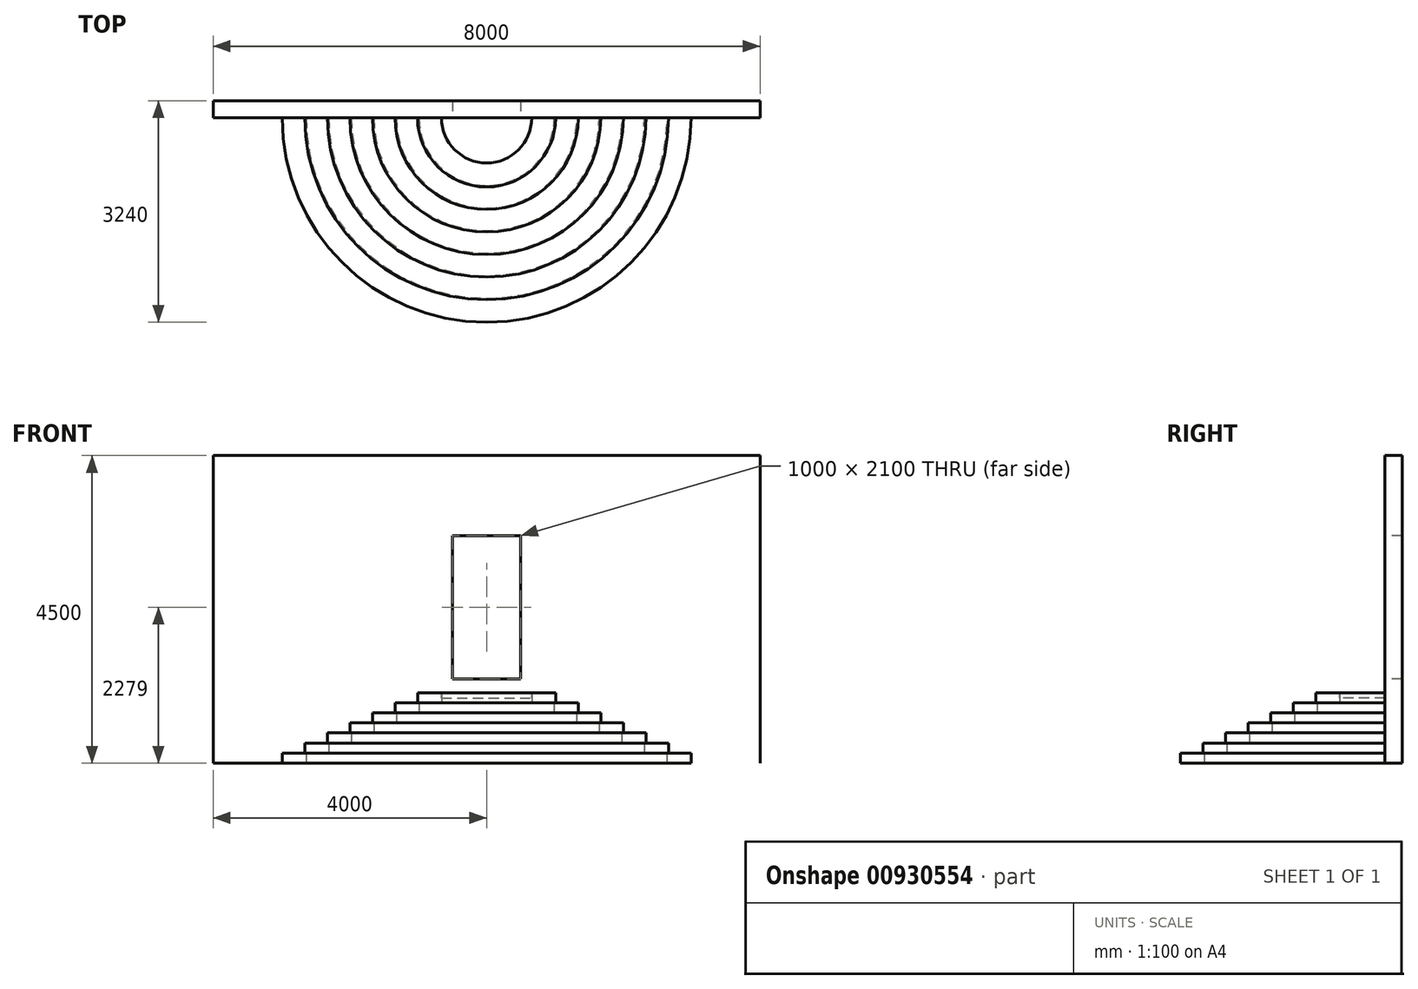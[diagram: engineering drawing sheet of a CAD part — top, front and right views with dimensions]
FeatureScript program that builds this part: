
annotation { "Feature Type Name" : "Feature", "Feature Type Description" : "" }
export const myFeature = defineFeature(function(context is Context, id is Id, definition is map)
    precondition{}
    {
        {
            var Q0;
            Q0=qCreatedBy(makeId("Top.planeOp"),FACE);
            var sketch = newSketch(context, id + "F0", { "sketchPlane" : qUnion([Q0])});
            skArc(sketch, "E0", {"start": v(-2990, 0) * mm, "mid": v(0, -2990) * mm, "end": v(2990, 0) * mm});
            skArc(sketch, "E1", {"start": v(-2640, 0) * mm, "mid": v(0, -2640) * mm, "end": v(2640, 0) * mm});
            skLineSegment(sketch, "E2", {"start": v(-2990, 0) * mm, "end": v(-2640, 0) * mm});
            skLineSegment(sketch, "E3", {"start": v(2640, 0) * mm, "end": v(2990, 0) * mm});
            skSolve(sketch);
        }
        {
            var Q0;
            Q0 = qSketchRegion(id + "F0", true);
            extrude(context, id + "F1", {"entities" : qUnion([Q0]), "depth" : 147 * mm, "offsetDistance" : 25 * mm});
        }
        {
            var Q0;
            Q0=makeQuery(id+"F1.opExtrude","CAP_FACE",FACE,{"disambiguationData":[OSD([sQuery(id+"F0.wireOp",EDGE,"E0"),sQuery(id+"F0.wireOp",EDGE,"E1"),sQuery(id+"F0.wireOp",EDGE,"E2"),sQuery(id+"F0.wireOp",EDGE,"E3")])],"isStart":false});
            var sketch = newSketch(context, id + "F2", { "sketchPlane" : qUnion([Q0])});
            skArc(sketch, "E4", {"start": v(-2660, 0) * mm, "mid": v(0, -2660) * mm, "end": v(2660, 0) * mm});
            skArc(sketch, "E5", {"start": v(-2310, 0) * mm, "mid": v(0, -2310) * mm, "end": v(2310, 0) * mm});
            skLineSegment(sketch, "E6", {"start": v(-2660, 0) * mm, "end": v(-2310, 0) * mm});
            skLineSegment(sketch, "E7", {"start": v(2310, 0) * mm, "end": v(2660, 0) * mm});
            skSolve(sketch);
        }
        {
            var Q0;
            Q0 = qSketchRegion(id + "F2", true);
            extrude(context, id + "F3", {"entities" : qUnion([Q0]), "operationType" : NewBodyOperationType.ADD, "depth" : 147 * mm, "offsetDistance" : 25 * mm});
        }
        {
            var Q0;
            Q0=makeQuery(id+"F3.opExtrude","CAP_FACE",FACE,{"disambiguationData":[OSD([sQuery(id+"F2.wireOp",EDGE,"E4"),sQuery(id+"F2.wireOp",EDGE,"E5"),sQuery(id+"F2.wireOp",EDGE,"E6"),sQuery(id+"F2.wireOp",EDGE,"E7")])],"isStart":false});
            var sketch = newSketch(context, id + "F4", { "sketchPlane" : qUnion([Q0])});
            skArc(sketch, "E8", {"start": v(-2330, 0) * mm, "mid": v(0, -2330) * mm, "end": v(2330, 0) * mm});
            skArc(sketch, "E9", {"start": v(-1980, 0) * mm, "mid": v(0, -1980) * mm, "end": v(1980, 0) * mm});
            skLineSegment(sketch, "E10", {"start": v(-2330, 0) * mm, "end": v(-1980, 0) * mm});
            skLineSegment(sketch, "E11", {"start": v(1980, 0) * mm, "end": v(2330, 0) * mm});
            skSolve(sketch);
        }
        {
            var Q0;
            Q0 = qSketchRegion(id + "F4", true);
            extrude(context, id + "F5", {"entities" : qUnion([Q0]), "operationType" : NewBodyOperationType.ADD, "depth" : 147 * mm, "offsetDistance" : 25 * mm});
        }
        {
            var Q0;
            Q0=makeQuery(id+"F5.opExtrude","CAP_FACE",FACE,{"disambiguationData":[OSD([sQuery(id+"F4.wireOp",EDGE,"E8"),sQuery(id+"F4.wireOp",EDGE,"E9"),sQuery(id+"F4.wireOp",EDGE,"E10"),sQuery(id+"F4.wireOp",EDGE,"E11")])],"isStart":false});
            var sketch = newSketch(context, id + "F6", { "sketchPlane" : qUnion([Q0])});
            skArc(sketch, "E12", {"start": v(-2000, 0) * mm, "mid": v(0, -2000) * mm, "end": v(2000, 0) * mm});
            skArc(sketch, "E13", {"start": v(-1650, 0) * mm, "mid": v(0, -1650) * mm, "end": v(1650, 0) * mm});
            skLineSegment(sketch, "E14", {"start": v(-2000, 0) * mm, "end": v(-1650, 0) * mm});
            skLineSegment(sketch, "E15", {"start": v(1650, 0) * mm, "end": v(2000, 0) * mm});
            skSolve(sketch);
        }
        {
            var Q0;
            Q0 = qSketchRegion(id + "F6", true);
            extrude(context, id + "F7", {"entities" : qUnion([Q0]), "operationType" : NewBodyOperationType.ADD, "depth" : 147 * mm, "offsetDistance" : 25 * mm});
        }
        {
            var Q0;
            Q0=makeQuery(id+"F7.opExtrude","CAP_FACE",FACE,{"disambiguationData":[OSD([sQuery(id+"F6.wireOp",EDGE,"E12"),sQuery(id+"F6.wireOp",EDGE,"E13"),sQuery(id+"F6.wireOp",EDGE,"E14"),sQuery(id+"F6.wireOp",EDGE,"E15")])],"isStart":false});
            var sketch = newSketch(context, id + "F8", { "sketchPlane" : qUnion([Q0])});
            skArc(sketch, "E16", {"start": v(-1670, 0) * mm, "mid": v(0, -1670) * mm, "end": v(1670, 0) * mm});
            skArc(sketch, "E17", {"start": v(-1320, 0) * mm, "mid": v(0, -1320) * mm, "end": v(1320, 0) * mm});
            skLineSegment(sketch, "E18", {"start": v(-1670, 0) * mm, "end": v(-1320, 0) * mm});
            skLineSegment(sketch, "E19", {"start": v(1320, 0) * mm, "end": v(1670, 0) * mm});
            skSolve(sketch);
        }
        {
            var Q0;
            Q0 = qSketchRegion(id + "F8", true);
            extrude(context, id + "F9", {"entities" : qUnion([Q0]), "operationType" : NewBodyOperationType.ADD, "depth" : 147 * mm, "offsetDistance" : 25 * mm});
        }
        {
            var Q0;
            Q0=makeQuery(id+"F9.opExtrude","CAP_FACE",FACE,{"disambiguationData":[OSD([sQuery(id+"F8.wireOp",EDGE,"E16"),sQuery(id+"F8.wireOp",EDGE,"E17"),sQuery(id+"F8.wireOp",EDGE,"E18"),sQuery(id+"F8.wireOp",EDGE,"E19")])],"isStart":false});
            var sketch = newSketch(context, id + "F10", { "sketchPlane" : qUnion([Q0])});
            skArc(sketch, "E20", {"start": v(-1340, 0) * mm, "mid": v(0, -1340) * mm, "end": v(1340, 0) * mm});
            skArc(sketch, "E21", {"start": v(-990, 0) * mm, "mid": v(0, -990) * mm, "end": v(990, 0) * mm});
            skLineSegment(sketch, "E22", {"start": v(-1340, 0) * mm, "end": v(-990, 0) * mm});
            skLineSegment(sketch, "E23", {"start": v(990, 0) * mm, "end": v(1340, 0) * mm});
            skSolve(sketch);
        }
        {
            var Q0;
            Q0 = qSketchRegion(id + "F10", true);
            extrude(context, id + "F11", {"entities" : qUnion([Q0]), "operationType" : NewBodyOperationType.ADD, "depth" : 147 * mm, "offsetDistance" : 25 * mm});
        }
        {
            var Q0;
            Q0=makeQuery(id+"F11.opExtrude","CAP_FACE",FACE,{"disambiguationData":[OSD([sQuery(id+"F10.wireOp",EDGE,"E20"),sQuery(id+"F10.wireOp",EDGE,"E21"),sQuery(id+"F10.wireOp",EDGE,"E22"),sQuery(id+"F10.wireOp",EDGE,"E23")])],"isStart":false});
            var sketch = newSketch(context, id + "F12", { "sketchPlane" : qUnion([Q0])});
            skArc(sketch, "E24", {"start": v(-1010, 0) * mm, "mid": v(0, -1010) * mm, "end": v(1010, 0) * mm});
            skArc(sketch, "E25", {"start": v(-660, 0) * mm, "mid": v(0, -660) * mm, "end": v(660, 0) * mm});
            skLineSegment(sketch, "E26", {"start": v(-1010, 0) * mm, "end": v(-660, 0) * mm});
            skLineSegment(sketch, "E27", {"start": v(660, 0) * mm, "end": v(1010, 0) * mm});
            skSolve(sketch);
        }
        {
            var Q0;
            Q0 = qSketchRegion(id + "F12", true);
            extrude(context, id + "F13", {"entities" : qUnion([Q0]), "operationType" : NewBodyOperationType.ADD, "depth" : 147 * mm, "offsetDistance" : 25 * mm});
        }
        {
            var Q0;
            Q0=makeQuery(id+"F13.opExtrude","CAP_FACE",FACE,{"disambiguationData":[OSD([sQuery(id+"F12.wireOp",EDGE,"E24"),sQuery(id+"F12.wireOp",EDGE,"E25"),sQuery(id+"F12.wireOp",EDGE,"E26"),sQuery(id+"F12.wireOp",EDGE,"E27")])],"isStart":false});
            var sketch = newSketch(context, id + "F14", { "sketchPlane" : qUnion([Q0])});
            skArc(sketch, "E28", {"start": v(-660, 0) * mm, "mid": v(0, -660) * mm, "end": v(660, 0) * mm});
            skLineSegment(sketch, "E29", {"start": v(-660, 0) * mm, "end": v(660, 0) * mm});
            skSolve(sketch);
        }
        {
            var Q0;
            Q0 = qSketchRegion(id + "F14", true);
            extrude(context, id + "F15", {"entities" : qUnion([Q0]), "oppositeDirection" : true, "depth" : 80 * mm, "offsetDistance" : 25 * mm});
        }
        {
            var Q0;
            Q0=qCreatedBy(makeId("Front.planeOp"),FACE);
            var sketch = newSketch(context, id + "F16", { "sketchPlane" : qUnion([Q0])});
            skLineSegment(sketch, "E30.bottom", {"start": v(-4000, 0) * mm, "end": v(4000, 0) * mm});
            skLineSegment(sketch, "E30.top", {"start": v(-4000, 4500) * mm, "end": v(4000, 4500) * mm});
            skLineSegment(sketch, "E30.left", {"start": v(-4000, 0) * mm, "end": v(-4000, 4500) * mm});
            skLineSegment(sketch, "E30.right", {"start": v(4000, 0) * mm, "end": v(4000, 4500) * mm});
            skLineSegment(sketch, "E31.bottom", {"start": v(-500, 1229) * mm, "end": v(500, 1229) * mm});
            skLineSegment(sketch, "E31.top", {"start": v(-500, 3329) * mm, "end": v(500, 3329) * mm});
            skLineSegment(sketch, "E31.left", {"start": v(-500, 1229) * mm, "end": v(-500, 3329) * mm});
            skLineSegment(sketch, "E31.right", {"start": v(500, 1229) * mm, "end": v(500, 3329) * mm});
            skLineSegment(sketch, "E32", {"start": v(0, 1229) * mm, "end": v(0, 0) * mm, "construction": true});
            skSolve(sketch);
        }
        {
            var Q0;
            Q0 = qSketchRegion(id + "F16", true);
            extrude(context, id + "F17", {"entities" : qUnion([Q0]), "oppositeDirection" : true, "depth" : 250 * mm, "offsetDistance" : 25 * mm});
        }
    });
